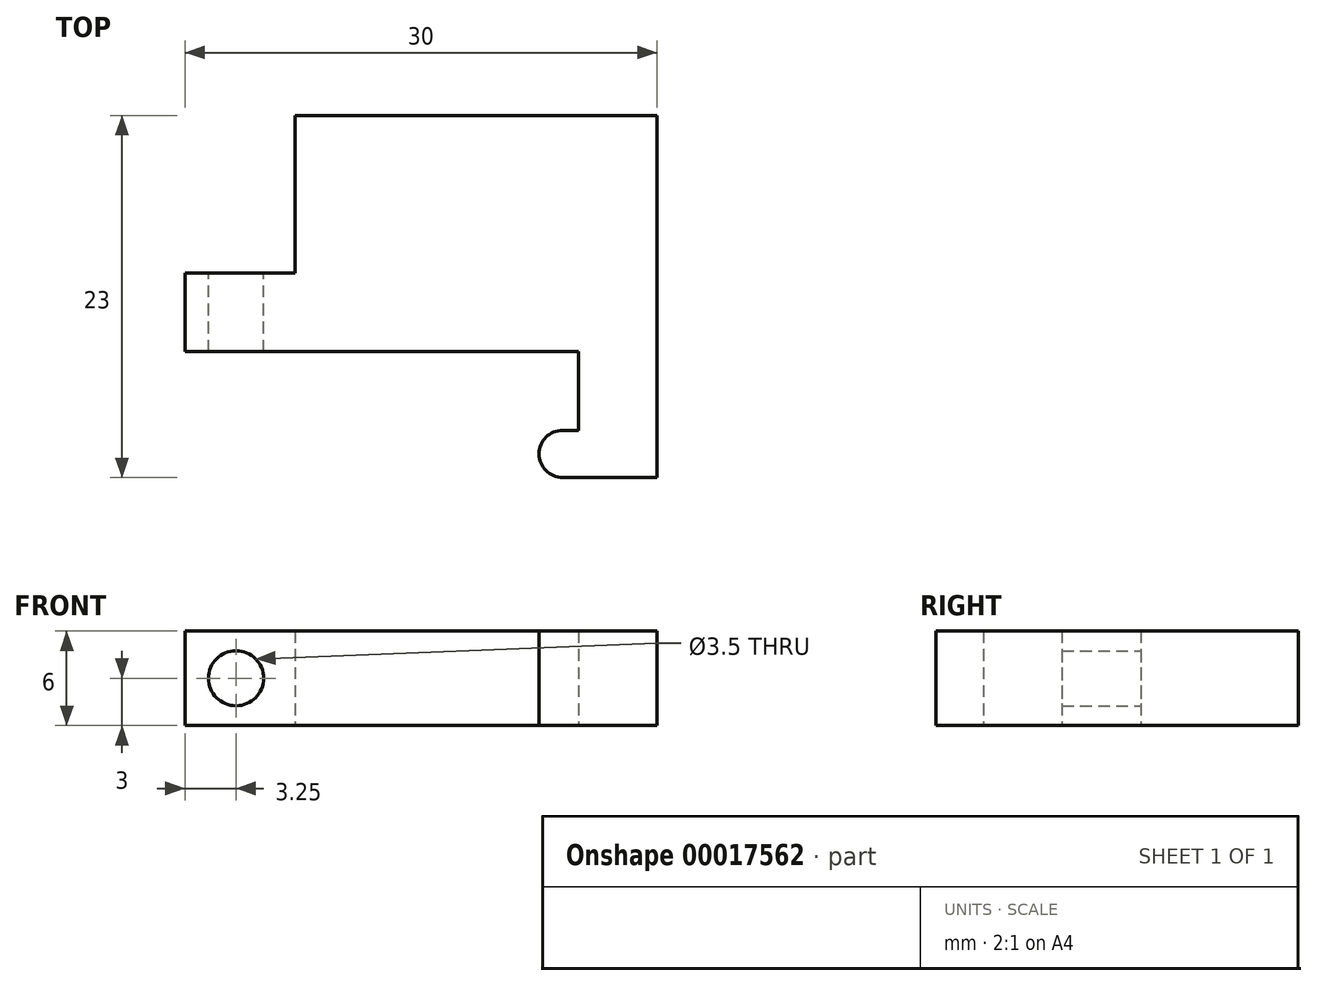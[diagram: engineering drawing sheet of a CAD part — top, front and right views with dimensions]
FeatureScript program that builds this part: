
annotation { "Feature Type Name" : "Feature", "Feature Type Description" : "" }
export const myFeature = defineFeature(function(context is Context, id is Id, definition is map)
    precondition{}
    {
        {
            var Q0;
            Q0=qCreatedBy(makeId("Top.planeOp"),FACE);
            var sketch = newSketch(context, id + "F0", { "sketchPlane" : qUnion([Q0])});
            skLineSegment(sketch, "E0", {"start": v(0, 0) * mm, "end": v(5, 0) * mm});
            skLineSegment(sketch, "E1", {"start": v(5, 0) * mm, "end": v(5, 13) * mm});
            skLineSegment(sketch, "E2", {"start": v(5, 13) * mm, "end": v(-25, 13) * mm});
            skLineSegment(sketch, "E3", {"start": v(-25, 13) * mm, "end": v(-25, 8) * mm});
            skLineSegment(sketch, "E4", {"start": v(-25, 8) * mm, "end": v(0, 8) * mm});
            skLineSegment(sketch, "E5", {"start": v(0, 8) * mm, "end": v(0, 3) * mm});
            skLineSegment(sketch, "E6", {"start": v(0, 3) * mm, "end": v(-1, 3) * mm});
            skLineSegment(sketch, "E7", {"start": v(0, 0) * mm, "end": v(-1, 0) * mm});
            skArc(sketch, "E8", {"start": v(-1, 3) * mm, "mid": v(-2.5, 1.5) * mm, "end": v(-1, 0) * mm});
            skSolve(sketch);
        }
        {
            var Q0;
            Q0=qSketchRegion(id+"F0",true);
            extrude(context, id + "F1", {"entities" : qUnion([Q0]), "depth" : 6 * mm});
        }
        {
            var Q0;
            Q0=makeQuery(id+"F1.opExtrude","SWEPT_FACE",FACE,{"disambiguationData":[OSD([sQuery(id+"F0.wireOp",EDGE,"E2")])]});
            var sketch = newSketch(context, id + "F2", { "sketchPlane" : qUnion([Q0])});
            skCircle(sketch, "E9", {"center": v(21.75, 3) * mm, "radius": 1.75 * mm});
            skLineSegment(sketch, "E10", {"start": v(21.75, 6) * mm, "end": v(21.75, 0) * mm});
            skSolve(sketch);
        }
        {
            var Q0;
            Q0=qSketchRegion(id+"F2",true);
            extrude(context, id + "F3", {"entities" : qUnion([Q0]), "operationType" : NewBodyOperationType.REMOVE, "oppositeDirection" : true, "depth" : 25 * mm});
        }
        {
            var Q0;
            Q0=makeQuery(id+"F1.opExtrude","SWEPT_FACE",FACE,{"disambiguationData":[OSD([sQuery(id+"F0.wireOp",EDGE,"E2")])]});
            var sketch = newSketch(context, id + "F4", { "sketchPlane" : qUnion([Q0])});
            skLineSegment(sketch, "E11.bottom", {"start": v(-5, 6) * mm, "end": v(18, 6) * mm});
            skLineSegment(sketch, "E11.top", {"start": v(-5, 0) * mm, "end": v(18, 0) * mm});
            skLineSegment(sketch, "E11.left", {"start": v(-5, 6) * mm, "end": v(-5, 0) * mm});
            skLineSegment(sketch, "E11.right", {"start": v(18, 6) * mm, "end": v(18, 0) * mm});
            skSolve(sketch);
        }
        {
            var Q0;
            Q0=qSketchRegion(id+"F4",true);
            extrude(context, id + "F5", {"entities" : qUnion([Q0]), "operationType" : NewBodyOperationType.ADD, "depth" : 10 * mm});
        }
    });
